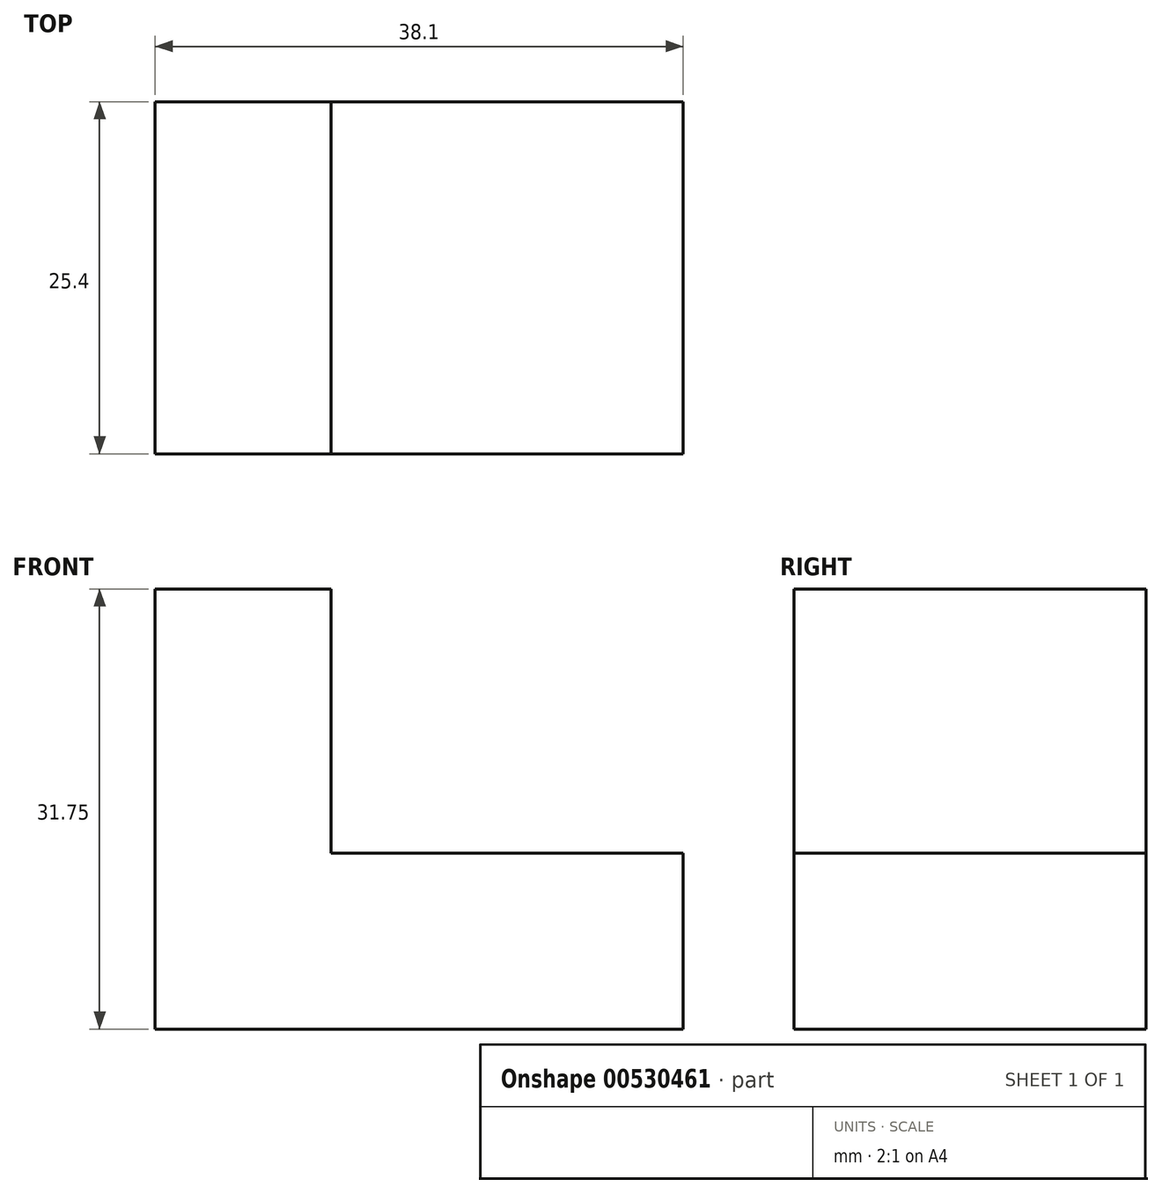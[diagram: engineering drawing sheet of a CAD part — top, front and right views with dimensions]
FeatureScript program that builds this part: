
annotation { "Feature Type Name" : "Feature", "Feature Type Description" : "" }
export const myFeature = defineFeature(function(context is Context, id is Id, definition is map)
    precondition{}
    {
        {
            var Q0;
            Q0=qCreatedBy(makeId("Front.planeOp"),FACE);
            var sketch = newSketch(context, id + "F0", { "sketchPlane" : qUnion([Q0])});
            skLineSegment(sketch, "E0", {"start": v(-59.82, 0) * mm, "end": v(-59.82, 31.75) * mm});
            skLineSegment(sketch, "E1", {"start": v(-59.82, 31.75) * mm, "end": v(-47.12, 31.75) * mm});
            skLineSegment(sketch, "E2", {"start": v(-47.12, 31.75) * mm, "end": v(-47.12, 12.7) * mm});
            skLineSegment(sketch, "E3", {"start": v(-47.12, 12.7) * mm, "end": v(-21.72, 12.7) * mm});
            skLineSegment(sketch, "E4", {"start": v(-21.72, 12.7) * mm, "end": v(-21.72, 0) * mm});
            skLineSegment(sketch, "E5", {"start": v(-59.82, 0) * mm, "end": v(-21.72, 0) * mm});
            skSolve(sketch);
        }
        {
            var Q0;
            Q0=makeQuery(id+"F0.imprint","IMPRINT",FACE,{"disambiguationData":[TD([[makeQuery(id+"F0.imprint","IMPRINT",EDGE,{"derivedFrom":sQuery(id+"F0.wireOp",EDGE,"E0")}),-1.0]])]});
            extrude(context, id + "F1", {"entities" : qUnion([Q0]), "depth" : 25.4 * mm, "offsetDistance" : 25.4 * mm});
        }
    });
